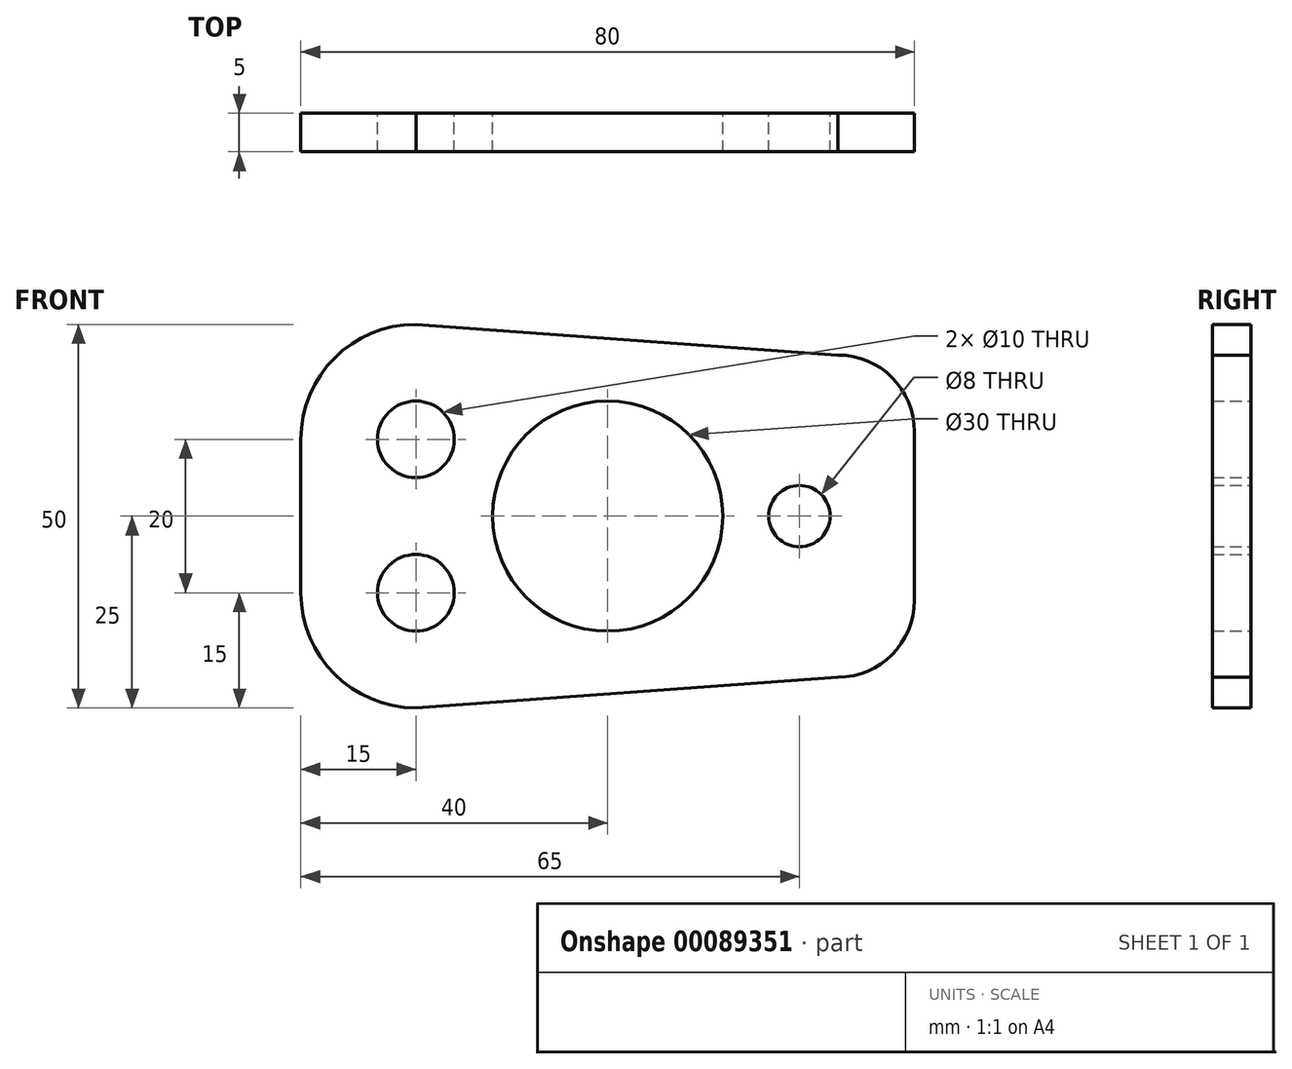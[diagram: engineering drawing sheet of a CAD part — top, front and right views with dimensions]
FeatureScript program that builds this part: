
annotation { "Feature Type Name" : "Feature", "Feature Type Description" : "" }
export const myFeature = defineFeature(function(context is Context, id is Id, definition is map)
    precondition{}
    {
        {
            var Q0;
            Q0=qCreatedBy(makeId("Front.planeOp"),FACE);
            var sketch = newSketch(context, id + "F0", { "sketchPlane" : qUnion([Q0])});
            skCircle(sketch, "E0", {"center": v(0, 0) * mm, "radius": 15 * mm});
            skCircle(sketch, "E1", {"center": v(25, 0) * mm, "radius": 4 * mm});
            skLineSegment(sketch, "E2", {"start": v(-59.43, 0) * mm, "end": v(101.23, 0) * mm, "construction": true});
            skLineSegment(sketch, "E3", {"start": v(-25, -28.52) * mm, "end": v(-25, 34.79) * mm, "construction": true});
            skLineSegment(sketch, "E4", {"start": v(0, -26.86) * mm, "end": v(0, 36.66) * mm, "construction": true});
            skLineSegment(sketch, "E5", {"start": v(-40, 0) * mm, "end": v(-40, 10) * mm});
            skLineSegment(sketch, "E6", {"start": v(-40, 0) * mm, "end": v(-40, -10) * mm});
            skLineSegment(sketch, "E7", {"start": v(40, 0) * mm, "end": v(40, 11) * mm});
            skLineSegment(sketch, "E8", {"start": v(40, 0) * mm, "end": v(40, -11) * mm});
            skCircle(sketch, "E9", {"center": v(-25, 10) * mm, "radius": 5 * mm});
            skCircle(sketch, "E10", {"center": v(-25, -10) * mm, "radius": 5 * mm});
            skLineSegment(sketch, "E11", {"start": v(-40, -10) * mm, "end": v(-20, -10) * mm, "construction": true});
            skLineSegment(sketch, "E12", {"start": v(-40, 10) * mm, "end": v(-20, 10) * mm, "construction": true});
            skArc(sketch, "E13", {"start": v(-40, 10) * mm, "mid": v(-35.6, 20.6) * mm, "end": v(-25, 25) * mm});
            skLineSegment(sketch, "E14", {"start": v(25, -10.27) * mm, "end": v(25, 43.57) * mm, "construction": true});
            skArc(sketch, "E15", {"start": v(-40, -10) * mm, "mid": v(-35.6, -20.6) * mm, "end": v(-25, -25) * mm});
            skArc(sketch, "E16", {"start": v(40, 11) * mm, "mid": v(37.07, 18.07) * mm, "end": v(30, 21) * mm});
            skArc(sketch, "E17", {"start": v(40, -11) * mm, "mid": v(37.07, -18.07) * mm, "end": v(30, -21) * mm});
            skLineSegment(sketch, "E18", {"start": v(-25, 25) * mm, "end": v(30, 21) * mm});
            skLineSegment(sketch, "E19", {"start": v(-25, -25) * mm, "end": v(30, -21) * mm});
            skSolve(sketch);
        }
        {
            var Q0;
            Q0 = qSketchRegion(id + "F0", true);
            extrude(context, id + "F1", {"entities" : qUnion([Q0]), "depth" : 5 * mm});
        }
    });
